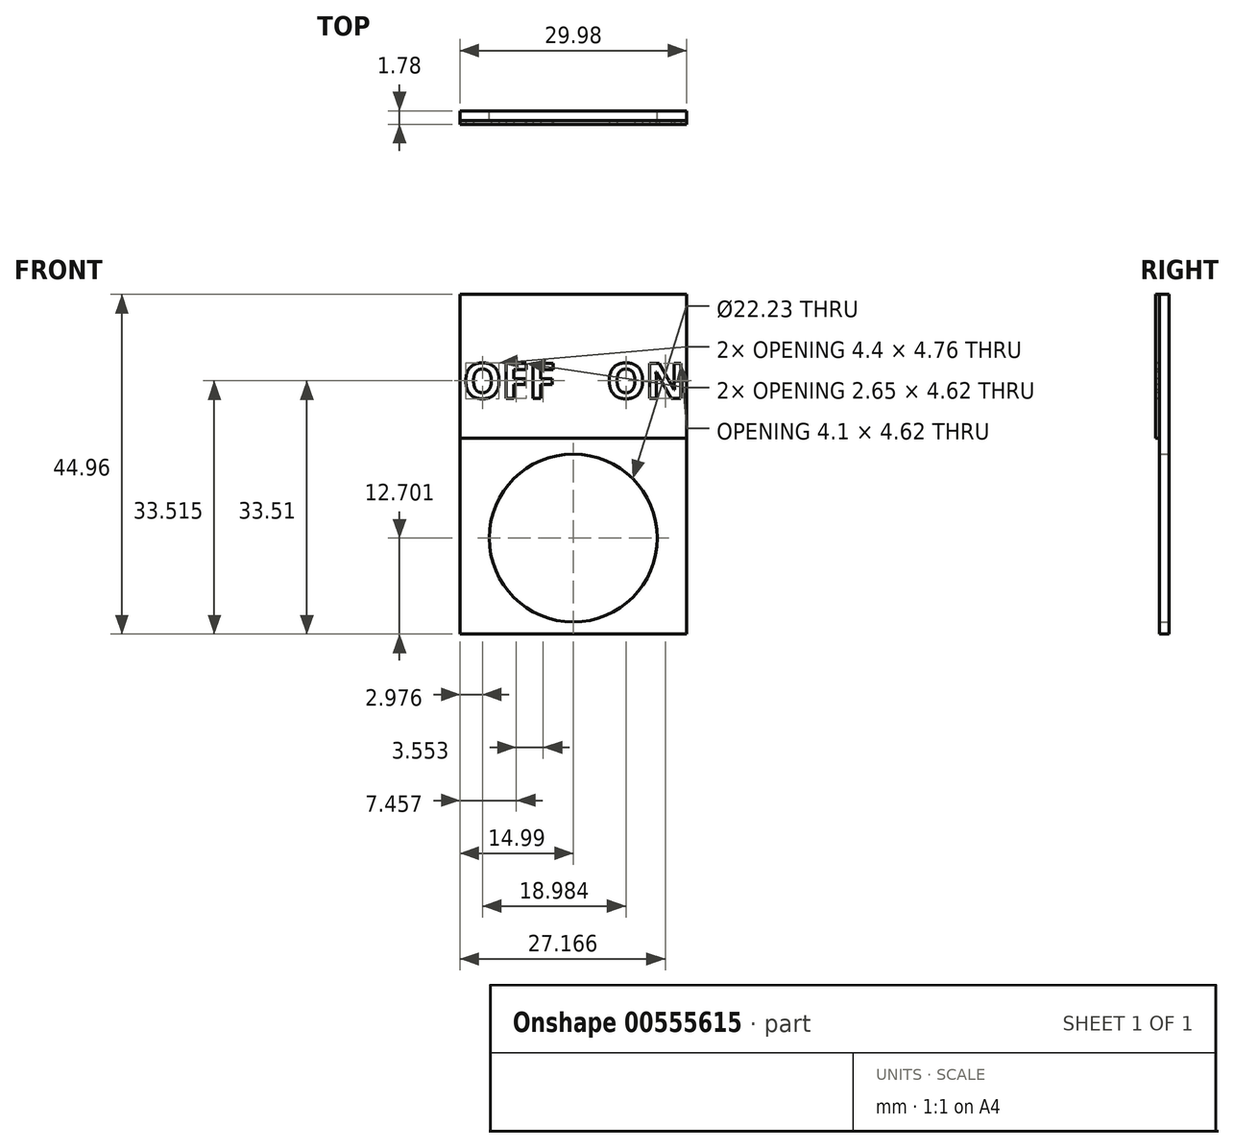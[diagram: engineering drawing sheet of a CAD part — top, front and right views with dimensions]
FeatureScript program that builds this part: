
annotation { "Feature Type Name" : "Feature", "Feature Type Description" : "" }
export const myFeature = defineFeature(function(context is Context, id is Id, definition is map)
    precondition{}
    {
        {
            var Q0;
            Q0=qCreatedBy(makeId("Front.planeOp"),FACE);
            var sketch = newSketch(context, id + "F0", { "sketchPlane" : qUnion([Q0])});
            skLineSegment(sketch, "E0.bottom", {"start": v(14.99, 22.48) * mm, "end": v(-14.99, 22.48) * mm});
            skLineSegment(sketch, "E0.top", {"start": v(14.99, -22.48) * mm, "end": v(-14.99, -22.48) * mm});
            skLineSegment(sketch, "E0.left", {"start": v(14.99, 22.48) * mm, "end": v(14.99, -22.48) * mm});
            skLineSegment(sketch, "E0.right", {"start": v(-14.99, 22.48) * mm, "end": v(-14.99, -22.48) * mm});
            skPoint(sketch, "E0.middle", {"position": v(0, 0) * mm});
            skCircle(sketch, "E1", {"center": v(0, -9.78) * mm, "radius": 11.11 * mm});
            skPoint(sketch, "E1.centerSnap0", {"position": v(0, -22.48) * mm});
            skSolve(sketch);
        }
        {
            var Q0;
            Q0 = qSketchRegion(id + "F0", true);
            extrude(context, id + "F1", {"entities" : qUnion([Q0]), "depth" : 1.27 * mm, "offsetDistance" : 25.4 * mm});
        }
        {
            var Q0;
            Q0=makeQuery(id+"F1.opExtrude","CAP_FACE",FACE,{"disambiguationData":[OSD([sQuery(id+"F0.wireOp",EDGE,"E0.bottom"),sQuery(id+"F0.wireOp",EDGE,"E0.top"),sQuery(id+"F0.wireOp",EDGE,"E0.left"),sQuery(id+"F0.wireOp",EDGE,"E0.right"),sQuery(id+"F0.wireOp",EDGE,"E1")])],"isStart":false});
            var sketch = newSketch(context, id + "F2", { "sketchPlane" : qUnion([Q0])});
            skLineSegment(sketch, "E2.bottom", {"start": v(-14.99, 22.48) * mm, "end": v(14.99, 22.48) * mm});
            skLineSegment(sketch, "E2.top", {"start": v(-14.99, 3.43) * mm, "end": v(14.99, 3.43) * mm});
            skLineSegment(sketch, "E2.left", {"start": v(-14.99, 22.48) * mm, "end": v(-14.99, 3.43) * mm});
            skLineSegment(sketch, "E2.right", {"start": v(14.99, 22.48) * mm, "end": v(14.99, 3.43) * mm});
            skSolve(sketch);
        }
        {
            var Q0;
            Q0 = qSketchRegion(id + "F2", true);
            extrude(context, id + "F3", {"entities" : qUnion([Q0]), "depth" : 0.5 * mm, "offsetDistance" : 25.4 * mm});
        }
        {
            var Q0;
            Q0=makeQuery(id+"F3.opExtrude","CAP_FACE",FACE,{"disambiguationData":[OSD([sQuery(id+"F2.wireOp",EDGE,"E2.bottom"),sQuery(id+"F2.wireOp",EDGE,"E2.top"),sQuery(id+"F2.wireOp",EDGE,"E2.left"),sQuery(id+"F2.wireOp",EDGE,"E2.right")])],"isStart":false});
            var sketch = newSketch(context, id + "F4", { "sketchPlane" : qUnion([Q0])});
            skText(sketch, "E3", { "text": "OFF    ON", "fontName": "OpenSans-Bold.ttf"});
            const initialGuessF4  = {"E3": [-0.01459, 0.00872, 1, 0, 0.00466]};
            skSetInitialGuess(sketch, initialGuessF4);
            skSolve(sketch);
        }
        {
            var Q0;
            Q0 = qSketchRegion(id + "F4", true);
            extrude(context, id + "F5", {"entities" : qUnion([Q0]), "operationType" : NewBodyOperationType.REMOVE, "oppositeDirection" : true, "depth" : 0.5 * mm, "offsetDistance" : 25.4 * mm});
        }
    });
